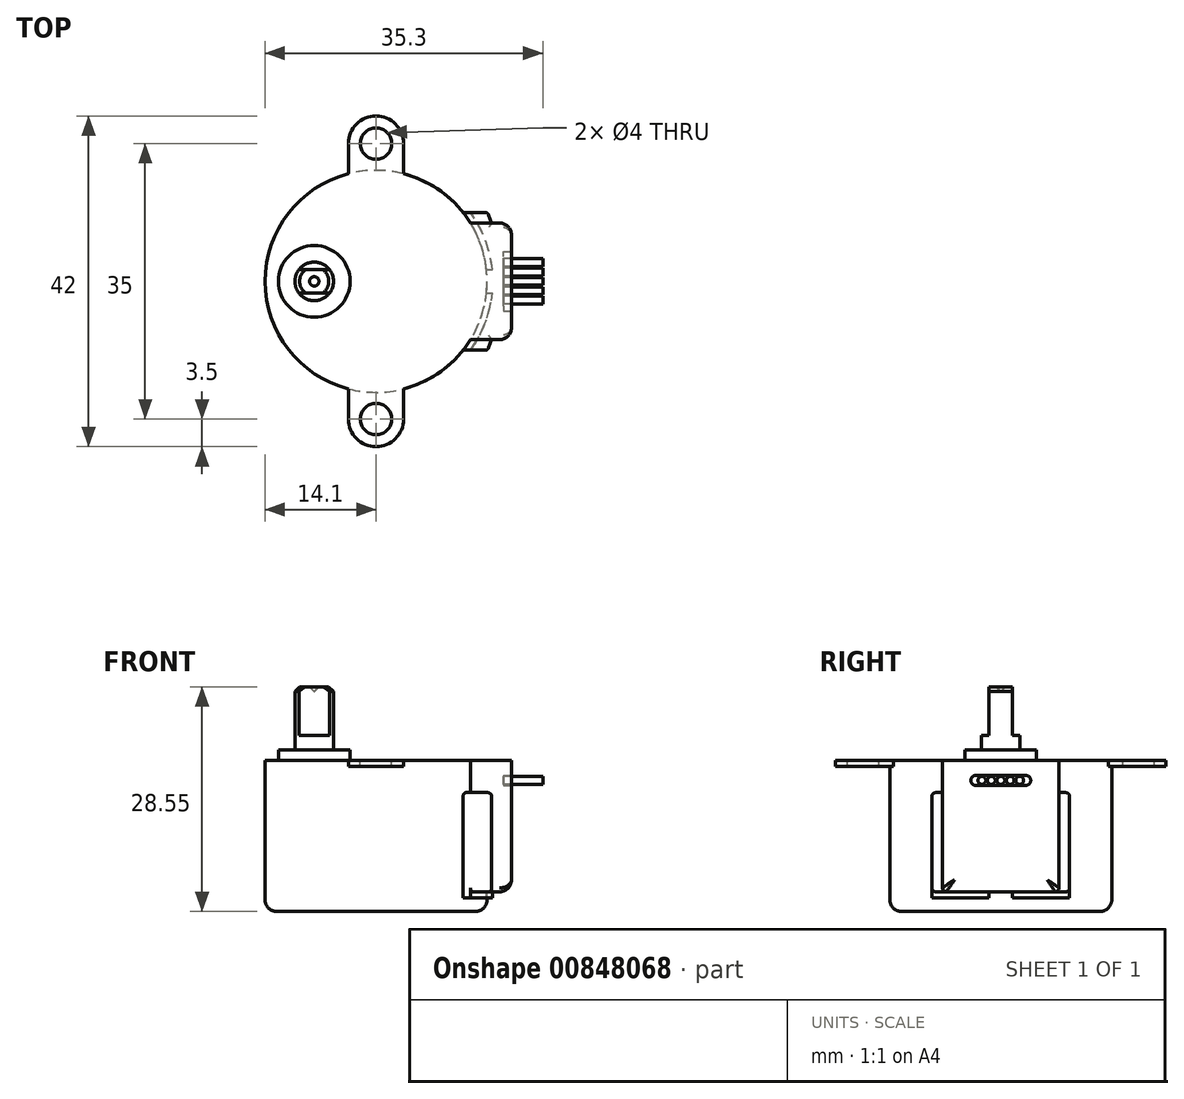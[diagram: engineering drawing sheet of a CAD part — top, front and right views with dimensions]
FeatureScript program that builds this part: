
annotation { "Feature Type Name" : "Feature", "Feature Type Description" : "" }
export const myFeature = defineFeature(function(context is Context, id is Id, definition is map)
    precondition{}
    {
        {
            var Q0;
            Q0=qCreatedBy(makeId("Front.planeOp"),FACE);
            var sketch = newSketch(context, id + "F0", { "sketchPlane" : qUnion([Q0])});
            skLineSegment(sketch, "E0", {"start": v(0, 0) * mm, "end": v(0, 8.75) * mm});
            skLineSegment(sketch, "E1", {"start": v(0.6, 9.35) * mm, "end": v(1.85, 9.35) * mm});
            skLineSegment(sketch, "E2", {"start": v(2.45, 8.75) * mm, "end": v(2.45, 1.35) * mm});
            skLineSegment(sketch, "E3", {"start": v(2.45, 1.35) * mm, "end": v(4.55, 1.35) * mm});
            skLineSegment(sketch, "E4", {"start": v(4.55, 1.35) * mm, "end": v(4.55, 0) * mm});
            skLineSegment(sketch, "E5", {"start": v(4.55, 0) * mm, "end": v(0, 0) * mm});
            skLineSegment(sketch, "E6", {"start": v(1.85, 9.35) * mm, "end": v(2.45, 8.75) * mm});
            skLineSegment(sketch, "E7", {"start": v(0.6, 9.35) * mm, "end": v(0, 8.75) * mm});
            skLineSegment(sketch, "E8", {"start": v(0, 8.75) * mm, "end": v(0, 13.35) * mm, "construction": true});
            skSolve(sketch);
        }
        {
            var Q0;
            Q0=makeQuery(id+"F0.imprint","IMPRINT",FACE,{"disambiguationData":[TD([[makeQuery(id+"F0.imprint","IMPRINT",EDGE,{"derivedFrom":sQuery(id+"F0.wireOp",EDGE,"E0")}),-1.0]])]});
            var Q1;
            Q1=sQuery(id+"F0.wireOp",EDGE,"E8");
            revolve(context, id + "F1", {"entities" : qUnion([Q0]), "axis" : qUnion([Q1]), "revolveType" : RevolveType.FULL, "surfaceOperationType" : NewSurfaceOperationType.NEW});
        }
        {
            var Q0;
            Q0=makeQuery(id+"F1.opRevolve","SWEPT_FACE",FACE,{"disambiguationData":[OSD([sQuery(id+"F0.wireOp",EDGE,"E1")])]});
            var sketch = newSketch(context, id + "F2", { "sketchPlane" : qUnion([Q0])});
            skLineSegment(sketch, "E9", {"start": v(-3.37, 1.5) * mm, "end": v(3.8, 1.5) * mm});
            skLineSegment(sketch, "E10", {"start": v(3.8, 1.5) * mm, "end": v(3.8, 4.5) * mm});
            skLineSegment(sketch, "E11", {"start": v(3.8, 4.5) * mm, "end": v(-3.37, 4.5) * mm});
            skLineSegment(sketch, "E12", {"start": v(-3.37, 4.5) * mm, "end": v(-3.37, 1.5) * mm});
            skLineSegment(sketch, "E13", {"start": v(0, 0) * mm, "end": v(9.16, 0) * mm, "construction": true});
            skLineSegment(sketch, "E14.MirrorCS", {"start": v(-3.37, -4.5) * mm, "end": v(-3.37, -1.5) * mm});
            skLineSegment(sketch, "E15.MirrorCS", {"start": v(3.8, -4.5) * mm, "end": v(-3.37, -4.5) * mm});
            skLineSegment(sketch, "E16.MirrorCS", {"start": v(3.8, -1.5) * mm, "end": v(3.8, -4.5) * mm});
            skLineSegment(sketch, "E17.MirrorCS", {"start": v(-3.37, -1.5) * mm, "end": v(3.8, -1.5) * mm});
            skSolve(sketch);
        }
        {
            var Q0;
            Q0=qSketchRegion(id+"F2",true);
            extrude(context, id + "F3", {"entities" : qUnion([Q0]), "operationType" : NewBodyOperationType.REMOVE, "oppositeDirection" : true, "depth" : 6.2 * mm});
        }
        {
            var Q0;
            Q0=makeQuery(id+"F1.opRevolve","SWEPT_FACE",FACE,{"disambiguationData":[OSD([sQuery(id+"F0.wireOp",EDGE,"E5")])]});
            var sketch = newSketch(context, id + "F4", { "sketchPlane" : qUnion([Q0])});
            skLineSegment(sketch, "E18", {"start": v(0, 0) * mm, "end": v(7.85, 0) * mm, "construction": true});
            skCircle(sketch, "E19", {"center": v(7.85, 0) * mm, "radius": 14.1 * mm});
            skLineSegment(sketch, "E20", {"start": v(0, 0) * mm, "end": v(-4.55, 0) * mm, "construction": true});
            skLineSegment(sketch, "E21", {"start": v(-4.55, 0) * mm, "end": v(-6.25, 0) * mm, "construction": true});
            skSolve(sketch);
        }
        {
            var Q0;
            Q0=qSketchRegion(id+"F4",true);
            extrude(context, id + "F5", {"entities" : qUnion([Q0]), "depth" : 19.2 * mm});
        }
        {
            var Q0;
            Q0=makeQuery(id+"F5.opExtrude","CAP_FACE",FACE,{"disambiguationData":[OSD([sQuery(id+"F0.wireOp",EDGE,"E4"),sQuery(id+"F0.wireOp",EDGE,"E5"),sQuery(id+"F4.wireOp",EDGE,"E19")])],"isStart":true});
            var sketch = newSketch(context, id + "F6", { "sketchPlane" : qUnion([Q0])});
            skLineSegment(sketch, "E22", {"start": v(7.85, 0) * mm, "end": v(7.85, 17.5) * mm, "construction": true});
            skCircle(sketch, "E23", {"center": v(7.85, 17.5) * mm, "radius": 2 * mm});
            skArc(sketch, "E24", {"start": v(11.35, 17.5) * mm, "mid": v(7.85, 21) * mm, "end": v(4.35, 17.5) * mm});
            skLineSegment(sketch, "E25", {"start": v(7.85, 0) * mm, "end": v(11.35, 0) * mm, "construction": true});
            skLineSegment(sketch, "E26", {"start": v(11.35, 0) * mm, "end": v(11.35, 17.5) * mm});
            skLineSegment(sketch, "E27", {"start": v(7.85, 0) * mm, "end": v(4.35, 0) * mm, "construction": true});
            skLineSegment(sketch, "E28", {"start": v(4.35, 0) * mm, "end": v(4.35, 17.5) * mm});
            skLineSegment(sketch, "E29.MirrorCS", {"start": v(4.35, 0) * mm, "end": v(4.35, -17.5) * mm});
            skArc(sketch, "E30.MirrorCS", {"start": v(11.35, -17.5) * mm, "mid": v(7.85, -21) * mm, "end": v(4.35, -17.5) * mm});
            skCircle(sketch, "E31.MirrorC", {"center": v(7.85, -17.5) * mm, "radius": 2 * mm});
            skLineSegment(sketch, "E32.MirrorCS", {"start": v(11.35, 0) * mm, "end": v(11.35, -17.5) * mm});
            skSolve(sketch);
        }
        {
            var Q0;
            Q0=qSketchRegion(id+"F6",true);
            extrude(context, id + "F7", {"entities" : qUnion([Q0]), "oppositeDirection" : true, "depth" : 0.75 * mm});
        }
        {
            var Q0;
            Q0=makeQuery(id+"F7.opExtrude","SWEPT_BODY",BODY,{"disambiguationData":[OSD([sQuery(id+"F6.wireOp",EDGE,"E23"),sQuery(id+"F6.wireOp",EDGE,"E24"),sQuery(id+"F6.wireOp",EDGE,"E26"),sQuery(id+"F6.wireOp",EDGE,"E28"),sQuery(id+"F6.wireOp",EDGE,"E29.MirrorCS"),sQuery(id+"F6.wireOp",EDGE,"E32.MirrorCS"),sQuery(id+"F6.wireOp",EDGE,"E30.MirrorCS"),sQuery(id+"F6.wireOp",EDGE,"E31.MirrorC")])]});
            var Q1;
            Q1=makeQuery(id+"F5.opExtrude","SWEPT_BODY",BODY,{"disambiguationData":[OSD([sQuery(id+"F0.wireOp",EDGE,"E4"),sQuery(id+"F0.wireOp",EDGE,"E5"),sQuery(id+"F4.wireOp",EDGE,"E19")])]});
            booleanBodies(context, id + "F8", {"operationType" : BooleanOperationType.UNION, "tools" : qUnion([Q0, Q1])});
        }
        {
            var Q0;
            Q0=makeQuery(id+"F8.opBoolean","MERGE",FACE,{"derivedFrom":[makeQuery(id+"F5.opExtrude","CAP_FACE",FACE,{"disambiguationData":[OSD([sQuery(id+"F4.wireOp",EDGE,"E19")])],"isStart":true}),makeQuery(id+"F7.opExtrude","CAP_FACE",FACE,{"disambiguationData":[OSD([sQuery(id+"F6.wireOp",EDGE,"E23"),sQuery(id+"F6.wireOp",EDGE,"E24"),sQuery(id+"F6.wireOp",EDGE,"E26"),sQuery(id+"F6.wireOp",EDGE,"E28"),sQuery(id+"F6.wireOp",EDGE,"E29.MirrorCS"),sQuery(id+"F6.wireOp",EDGE,"E32.MirrorCS"),sQuery(id+"F6.wireOp",EDGE,"E30.MirrorCS"),sQuery(id+"F6.wireOp",EDGE,"E31.MirrorC")])],"isStart":true})]});
            var sketch = newSketch(context, id + "F9", { "sketchPlane" : qUnion([Q0])});
            skLineSegment(sketch, "E33", {"start": v(7.85, 0) * mm, "end": v(25.05, 0) * mm, "construction": true});
            skPoint(sketch, "E33.endSnap0", {"position": v(21.95, 0) * mm});
            skLineSegment(sketch, "E34", {"start": v(25.05, 0) * mm, "end": v(25.05, 7.4) * mm});
            skLineSegment(sketch, "E35", {"start": v(25.05, 7.4) * mm, "end": v(7.85, 7.4) * mm});
            skLineSegment(sketch, "E36", {"start": v(7.85, 7.4) * mm, "end": v(7.85, 0) * mm});
            skLineSegment(sketch, "E37.MirrorCS", {"start": v(7.85, -7.4) * mm, "end": v(7.85, 0) * mm});
            skLineSegment(sketch, "E38.MirrorCS", {"start": v(25.05, -7.4) * mm, "end": v(7.85, -7.4) * mm});
            skLineSegment(sketch, "E39.MirrorCS", {"start": v(25.05, 0) * mm, "end": v(25.05, -7.4) * mm});
            skSolve(sketch);
        }
        {
            var Q0;
            {var subQ1=sQuery(id+"F9.wireOp",EDGE,"E34");Q0=makeQuery(id+"F9.imprint","IMPRINT",FACE,{"disambiguationData":[TD([[makeQuery(id+"F9.imprint","IMPRINT",EDGE,{"derivedFrom":subQ1}),1.0]])]});}
            extrude(context, id + "F10", {"entities" : qUnion([Q0]), "operationType" : NewBodyOperationType.ADD, "oppositeDirection" : true, "depth" : 16.7 * mm});
        }
        {
            var Q0;
            Q0=makeQuery(id+"F10.opExtrude","CAP_FACE",FACE,{"disambiguationData":[OSD([sQuery(id+"F4.wireOp",EDGE,"E19"),sQuery(id+"F9.wireOp",EDGE,"E34"),sQuery(id+"F9.wireOp",EDGE,"E35"),sQuery(id+"F9.wireOp",EDGE,"E38.MirrorCS"),sQuery(id+"F9.wireOp",EDGE,"E39.MirrorCS")])],"isStart":false});
            var sketch = newSketch(context, id + "F11", { "sketchPlane" : qUnion([Q0])});
            skLineSegment(sketch, "E40", {"start": v(25.05, 0) * mm, "end": v(21.95, 0) * mm, "construction": true});
            skLineSegment(sketch, "E41", {"start": v(22.55, 0) * mm, "end": v(22.55, 7.4) * mm});
            skLineSegment(sketch, "E42", {"start": v(22.55, 7.4) * mm, "end": v(22.05, 8.75) * mm});
            skLineSegment(sketch, "E43", {"start": v(22.05, 8.75) * mm, "end": v(18.9, 8.75) * mm});
            skLineSegment(sketch, "E44", {"start": v(18.9, 8.75) * mm, "end": v(18.9, 0) * mm});
            skLineSegment(sketch, "E45.MirrorCS", {"start": v(22.55, 0) * mm, "end": v(22.55, -7.4) * mm});
            skLineSegment(sketch, "E46.MirrorCS", {"start": v(22.55, -7.4) * mm, "end": v(22.05, -8.75) * mm});
            skLineSegment(sketch, "E47.MirrorCS", {"start": v(22.05, -8.75) * mm, "end": v(18.9, -8.75) * mm});
            skLineSegment(sketch, "E48.MirrorCS", {"start": v(18.9, -8.75) * mm, "end": v(18.9, 0) * mm});
            skSolve(sketch);
        }
        {
            var Q0;
            {var subQ3=sQuery(id+"F11.wireOp",EDGE,"E42");Q0=makeQuery(id+"F11.imprint","IMPRINT",FACE,{"disambiguationData":[TD([[makeQuery(id+"F11.imprint","IMPRINT",EDGE,{"derivedFrom":subQ3}),1.0]])]});}
            var Q1;
            {var subQ3=sQuery(id+"F11.wireOp",EDGE,"E41");Q1=makeQuery(id+"F11.imprint","IMPRINT",FACE,{"disambiguationData":[TD([[makeQuery(id+"F11.imprint","IMPRINT",EDGE,{"derivedFrom":subQ3}),1.0]])]});}
            extrude(context, id + "F12", {"entities" : qUnion([Q0, Q1]), "operationType" : NewBodyOperationType.ADD, "oppositeDirection" : true, "depth" : 12.6 * mm});
        }
        {
            var Q0;
            Q0=makeQuery(id+"F12.boolean.opBoolean","MERGE",FACE,{"derivedFrom":[makeQuery(id+"F10.opExtrude","CAP_FACE",FACE,{"disambiguationData":[OSD([sQuery(id+"F4.wireOp",EDGE,"E19"),sQuery(id+"F9.wireOp",EDGE,"E34"),sQuery(id+"F9.wireOp",EDGE,"E35"),sQuery(id+"F9.wireOp",EDGE,"E38.MirrorCS"),sQuery(id+"F9.wireOp",EDGE,"E39.MirrorCS")])],"isStart":false}),makeQuery(id+"F12.opExtrude","CAP_FACE",FACE,{"disambiguationData":[OSD([sQuery(id+"F11.wireOp",EDGE,"E41"),sQuery(id+"F11.wireOp",EDGE,"E42"),sQuery(id+"F11.wireOp",EDGE,"E43"),sQuery(id+"F11.wireOp",EDGE,"E44"),sQuery(id+"F11.wireOp",EDGE,"E45.MirrorCS"),sQuery(id+"F11.wireOp",EDGE,"E46.MirrorCS"),sQuery(id+"F11.wireOp",EDGE,"E47.MirrorCS"),sQuery(id+"F11.wireOp",EDGE,"E48.MirrorCS")])],"isStart":true})]});
            var sketch = newSketch(context, id + "F13", { "sketchPlane" : qUnion([Q0])});
            skLineSegment(sketch, "E49", {"start": v(25.05, 0) * mm, "end": v(7.85, 0) * mm, "construction": true});
            skArc(sketch, "E50", {"start": v(18.9, -8.75) * mm, "mid": v(20.9, -5.33) * mm, "end": v(21.87, -1.5) * mm});
            skArc(sketch, "E51", {"start": v(19.84, -8.75) * mm, "mid": v(21.71, -5.3) * mm, "end": v(22.62, -1.5) * mm});
            skLineSegment(sketch, "E52", {"start": v(18.9, -8.75) * mm, "end": v(19.84, -8.75) * mm});
            skLineSegment(sketch, "E53", {"start": v(21.87, -1.5) * mm, "end": v(22.62, -1.5) * mm});
            skLineSegment(sketch, "E54.MirrorCS", {"start": v(21.87, 1.5) * mm, "end": v(22.62, 1.5) * mm});
            skArc(sketch, "E55.MirrorCS", {"start": v(19.84, 8.75) * mm, "mid": v(21.71, 5.3) * mm, "end": v(22.62, 1.5) * mm});
            skArc(sketch, "E56.MirrorCS", {"start": v(18.9, 8.75) * mm, "mid": v(20.9, 5.33) * mm, "end": v(21.87, 1.5) * mm});
            skLineSegment(sketch, "E57.MirrorCS", {"start": v(18.9, 8.75) * mm, "end": v(19.84, 8.75) * mm});
            skSolve(sketch);
        }
        {
            var Q0;
            Q0=makeQuery(id+"F13.imprint","IMPRINT",FACE,{"disambiguationData":[TD([[makeQuery(id+"F13.imprint","IMPRINT",EDGE,{"derivedFrom":sQuery(id+"F13.wireOp",EDGE,"E50")}),-1.0]])]});
            var Q1;
            Q1=makeQuery(id+"F13.imprint","IMPRINT",FACE,{"disambiguationData":[TD([[makeQuery(id+"F13.imprint","IMPRINT",EDGE,{"derivedFrom":sQuery(id+"F13.wireOp",EDGE,"E54.MirrorCS")}),1.0]])]});
            extrude(context, id + "F14", {"entities" : qUnion([Q0, Q1]), "operationType" : NewBodyOperationType.ADD, "depth" : 0.75 * mm});
        }
        {
            var Q0;
            Q0=makeQuery(id+"F10.opExtrude","SWEPT_EDGE",EDGE,{"disambiguationData":[OSD([sQuery(id+"F9.wireOp",EDGE,"E38.MirrorCS"),sQuery(id+"F9.wireOp",EDGE,"E39.MirrorCS")])]});
            var Q1;
            Q1=makeQuery(id+"F10.opExtrude","SWEPT_EDGE",EDGE,{"disambiguationData":[OSD([sQuery(id+"F9.wireOp",EDGE,"E34"),sQuery(id+"F9.wireOp",EDGE,"E35")])]});
            var Q2;
            Q2=makeQuery(id+"F10.opExtrude","CAP_EDGE",EDGE,{"disambiguationData":[OSD([sQuery(id+"F9.wireOp",EDGE,"E34"),sQuery(id+"F9.wireOp",EDGE,"E39.MirrorCS")])],"isStart":false});
            var Q3;
            Q3=makeQuery(id+"F5.opExtrude","CAP_EDGE",EDGE,{"disambiguationData":[OSD([sQuery(id+"F4.wireOp",EDGE,"E19")])],"isStart":false});
            fillet(context, id + "F15", {"entities" : qUnion([Q0, Q1, Q2, Q3]), "radius" : 1.5 * mm, "tangentPropagation" : true, "allowEdgeOverflow" : false});
        }
        {
            var Q0;
            Q0=makeQuery(id+"F10.opExtrude","CAP_EDGE",EDGE,{"disambiguationData":[OSD([sQuery(id+"F9.wireOp",EDGE,"E35")])],"isStart":false});
            var Q1;
            Q1=makeQuery(id+"F12.opExtrude","CAP_EDGE",EDGE,{"disambiguationData":[OSD([sQuery(id+"F11.wireOp",EDGE,"E46.MirrorCS")])],"isStart":true});
            var Q2;
            Q2=makeQuery(id+"F12.opExtrude","CAP_EDGE",EDGE,{"disambiguationData":[OSD([sQuery(id+"F11.wireOp",EDGE,"E47.MirrorCS")])],"isStart":true});
            var Q3;
            Q3=makeQuery(id+"F12.opExtrude","SWEPT_EDGE",EDGE,{"disambiguationData":[OSD([sQuery(id+"F11.wireOp",EDGE,"E46.MirrorCS"),sQuery(id+"F11.wireOp",EDGE,"E47.MirrorCS")])]});
            var Q4;
            Q4=makeQuery(id+"F12.opExtrude","CAP_EDGE",EDGE,{"disambiguationData":[OSD([sQuery(id+"F11.wireOp",EDGE,"E46.MirrorCS")])],"isStart":false});
            var Q5;
            Q5=makeQuery(id+"F12.opExtrude","CAP_EDGE",EDGE,{"disambiguationData":[OSD([sQuery(id+"F11.wireOp",EDGE,"E47.MirrorCS")])],"isStart":false});
            var Q6;
            Q6=makeQuery(id+"F10.opExtrude","CAP_EDGE",EDGE,{"disambiguationData":[OSD([sQuery(id+"F9.wireOp",EDGE,"E38.MirrorCS")])],"isStart":false});
            var Q7;
            Q7=makeQuery(id+"F12.opExtrude","CAP_EDGE",EDGE,{"disambiguationData":[OSD([sQuery(id+"F11.wireOp",EDGE,"E42")])],"isStart":true});
            var Q8;
            Q8=makeQuery(id+"F12.opExtrude","CAP_EDGE",EDGE,{"disambiguationData":[OSD([sQuery(id+"F11.wireOp",EDGE,"E43")])],"isStart":true});
            var Q9;
            Q9=makeQuery(id+"F12.opExtrude","SWEPT_EDGE",EDGE,{"disambiguationData":[OSD([sQuery(id+"F11.wireOp",EDGE,"E42"),sQuery(id+"F11.wireOp",EDGE,"E43")])]});
            var Q10;
            Q10=makeQuery(id+"F12.opExtrude","CAP_EDGE",EDGE,{"disambiguationData":[OSD([sQuery(id+"F11.wireOp",EDGE,"E42")])],"isStart":false});
            var Q11;
            Q11=makeQuery(id+"F12.opExtrude","CAP_EDGE",EDGE,{"disambiguationData":[OSD([sQuery(id+"F11.wireOp",EDGE,"E43")])],"isStart":false});
            fillet(context, id + "F16", {"entities" : qUnion([Q0, Q1, Q2, Q3, Q4, Q5, Q6, Q7, Q8, Q9, Q10, Q11]), "radius" : 0.5 * mm, "tangentPropagation" : true, "allowEdgeOverflow" : false});
        }
        {
            var Q0;
            Q0=makeQuery(id+"F10.opExtrude","SWEPT_FACE",FACE,{"disambiguationData":[OSD([sQuery(id+"F9.wireOp",EDGE,"E34"),sQuery(id+"F9.wireOp",EDGE,"E39.MirrorCS")])]});
            var sketch = newSketch(context, id + "F17", { "sketchPlane" : qUnion([Q0])});
            skLineSegment(sketch, "E58", {"start": v(0, 0) * mm, "end": v(0, -2.55) * mm, "construction": true});
            skLineSegment(sketch, "E59", {"start": v(0, -2.55) * mm, "end": v(-3.15, -2.55) * mm, "construction": true});
            skArc(sketch, "E60", {"start": v(-3.15, -1.9) * mm, "mid": v(-3.8, -2.55) * mm, "end": v(-3.15, -3.2) * mm});
            skLineSegment(sketch, "E61", {"start": v(-3.15, -1.9) * mm, "end": v(0, -1.9) * mm});
            skPoint(sketch, "E61.endSnap0", {"position": v(0, -1.27) * mm});
            skLineSegment(sketch, "E62", {"start": v(-3.15, -3.2) * mm, "end": v(0, -3.2) * mm});
            skLineSegment(sketch, "E63.MirrorCS", {"start": v(3.15, -1.9) * mm, "end": v(0, -1.9) * mm});
            skArc(sketch, "E64.MirrorCS", {"start": v(3.15, -1.9) * mm, "mid": v(3.8, -2.55) * mm, "end": v(3.15, -3.2) * mm});
            skLineSegment(sketch, "E65.MirrorCS", {"start": v(3.15, -3.2) * mm, "end": v(0, -3.2) * mm});
            skSolve(sketch);
        }
        {
            var Q0;
            Q0=makeQuery(id+"F17.imprint","IMPRINT",FACE,{"disambiguationData":[TD([[makeQuery(id+"F17.imprint","IMPRINT",EDGE,{"derivedFrom":sQuery(id+"F17.wireOp",EDGE,"E60")}),1.0]])]});
            extrude(context, id + "F18", {"entities" : qUnion([Q0]), "operationType" : NewBodyOperationType.REMOVE, "oppositeDirection" : true, "depth" : 1 * mm});
        }
        {
            var Q0;
            Q0=makeQuery(id+"F18.boolean.opBoolean","COPY",FACE,{"derivedFrom":makeQuery(id+"F18.opExtrude","CAP_FACE",FACE,{"disambiguationData":[OSD([sQuery(id+"F17.wireOp",EDGE,"E60"),sQuery(id+"F17.wireOp",EDGE,"E61"),sQuery(id+"F17.wireOp",EDGE,"E62"),sQuery(id+"F17.wireOp",EDGE,"E63.MirrorCS"),sQuery(id+"F17.wireOp",EDGE,"E64.MirrorCS"),sQuery(id+"F17.wireOp",EDGE,"E65.MirrorCS")])],"isStart":false})});
            var sketch = newSketch(context, id + "F19", { "sketchPlane" : qUnion([Q0])});
            skLineSegment(sketch, "E66", {"start": v(0, -3.2) * mm, "end": v(0, -1.9) * mm, "construction": true});
            skLineSegment(sketch, "E67", {"start": v(0, -2.55) * mm, "end": v(1.2, -2.55) * mm, "construction": true});
            skLineSegment(sketch, "E68", {"start": v(1.2, -2.55) * mm, "end": v(2.4, -2.55) * mm, "construction": true});
            skLineSegment(sketch, "E69", {"start": v(0, -2.55) * mm, "end": v(-1.2, -2.55) * mm, "construction": true});
            skLineSegment(sketch, "E70", {"start": v(-1.2, -2.55) * mm, "end": v(-2.4, -2.55) * mm, "construction": true});
            skCircle(sketch, "E71", {"center": v(0, -2.55) * mm, "radius": 0.5 * mm});
            skCircle(sketch, "E72", {"center": v(-1.2, -2.55) * mm, "radius": 0.5 * mm});
            skCircle(sketch, "E73", {"center": v(-2.4, -2.55) * mm, "radius": 0.5 * mm});
            skCircle(sketch, "E74", {"center": v(1.2, -2.55) * mm, "radius": 0.5 * mm});
            skCircle(sketch, "E75", {"center": v(2.4, -2.55) * mm, "radius": 0.5 * mm});
            skSolve(sketch);
        }
        {
            var Q0;
            Q0=makeQuery(id+"F19.imprint","IMPRINT",FACE,{"disambiguationData":[TD([[makeQuery(id+"F19.imprint","IMPRINT",EDGE,{"derivedFrom":sQuery(id+"F19.wireOp",EDGE,"E73")}),1.0]])]});
            extrude(context, id + "F20", {"entities" : qUnion([Q0]), "depth" : 5 * mm});
        }
        {
            var Q0;
            Q0=makeQuery(id+"F19.imprint","IMPRINT",FACE,{"disambiguationData":[TD([[makeQuery(id+"F19.imprint","IMPRINT",EDGE,{"derivedFrom":sQuery(id+"F19.wireOp",EDGE,"E72")}),1.0]])]});
            extrude(context, id + "F21", {"entities" : qUnion([Q0]), "depth" : 5 * mm});
        }
        {
            var Q0;
            Q0=makeQuery(id+"F19.imprint","IMPRINT",FACE,{"disambiguationData":[TD([[makeQuery(id+"F19.imprint","IMPRINT",EDGE,{"derivedFrom":sQuery(id+"F19.wireOp",EDGE,"E71")}),1.0]])]});
            extrude(context, id + "F22", {"entities" : qUnion([Q0]), "depth" : 5 * mm});
        }
        {
            var Q0;
            Q0=makeQuery(id+"F19.imprint","IMPRINT",FACE,{"disambiguationData":[TD([[makeQuery(id+"F19.imprint","IMPRINT",EDGE,{"derivedFrom":sQuery(id+"F19.wireOp",EDGE,"E74")}),1.0]])]});
            extrude(context, id + "F23", {"entities" : qUnion([Q0]), "depth" : 5 * mm});
        }
        {
            var Q0;
            Q0=makeQuery(id+"F19.imprint","IMPRINT",FACE,{"disambiguationData":[TD([[makeQuery(id+"F19.imprint","IMPRINT",EDGE,{"derivedFrom":sQuery(id+"F19.wireOp",EDGE,"E75")}),1.0]])]});
            extrude(context, id + "F24", {"entities" : qUnion([Q0]), "depth" : 5 * mm});
        }
    });
